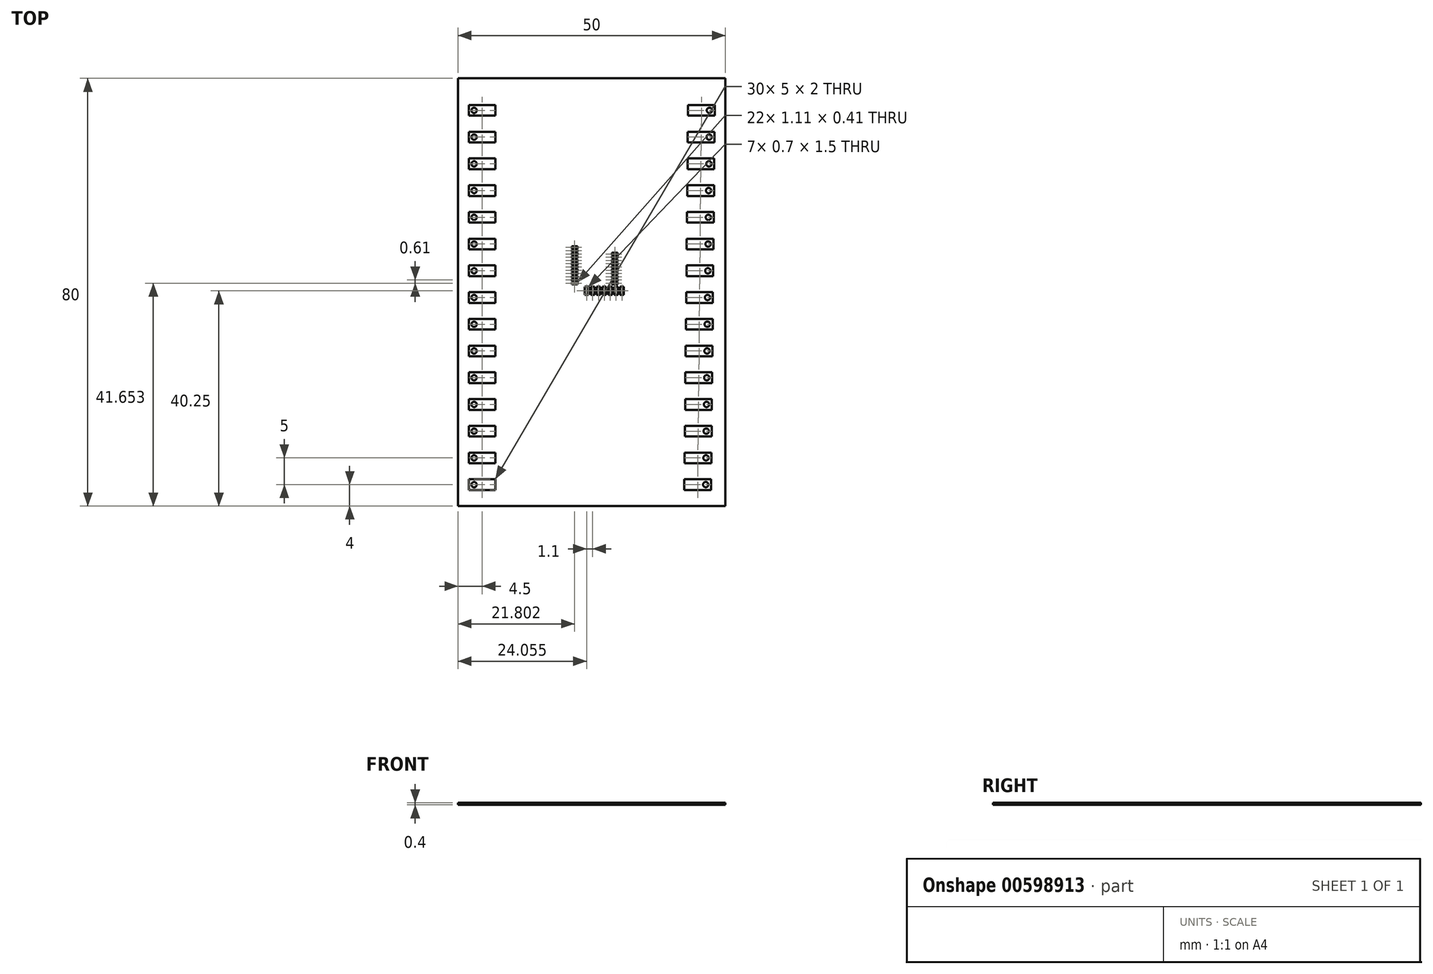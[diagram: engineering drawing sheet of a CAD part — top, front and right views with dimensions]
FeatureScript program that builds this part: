
annotation { "Feature Type Name" : "Feature", "Feature Type Description" : "" }
export const myFeature = defineFeature(function(context is Context, id is Id, definition is map)
    precondition{}
    {
        {
            var Q0;
            Q0=qCreatedBy(makeId("Top.planeOp"),FACE);
            var sketch = newSketch(context, id + "F0", { "sketchPlane" : qUnion([Q0])});
            skLineSegment(sketch, "E0.bottom", {"start": v(-25, 40) * mm, "end": v(25, 40) * mm});
            skLineSegment(sketch, "E0.top", {"start": v(-25, -40) * mm, "end": v(25, -40) * mm});
            skLineSegment(sketch, "E0.left", {"start": v(-25, 40) * mm, "end": v(-25, -40) * mm});
            skLineSegment(sketch, "E0.right", {"start": v(25, 40) * mm, "end": v(25, -40) * mm});
            skSolve(sketch);
        }
        {
            var Q0;
            Q0=makeQuery(id+"F0.imprint","IMPRINT",FACE,{"disambiguationData":[TD([[makeQuery(id+"F0.imprint","IMPRINT",EDGE,{"derivedFrom":sQuery(id+"F0.wireOp",EDGE,"E0.bottom")}),-1.0]])]});
            extrude(context, id + "F1", {"entities" : qUnion([Q0]), "depth" : .4 * mm, "offsetDistance" : 25 * mm});
        }
        {
            var Q0;
            Q0=makeQuery(id+"F1.opExtrude","CAP_FACE",FACE,{"disambiguationData":[OSD([sQuery(id+"F0.wireOp",EDGE,"E0.bottom"),sQuery(id+"F0.wireOp",EDGE,"E0.top"),sQuery(id+"F0.wireOp",EDGE,"E0.left"),sQuery(id+"F0.wireOp",EDGE,"E0.right")])],"isStart":false});
            var sketch = newSketch(context, id + "F2", { "sketchPlane" : qUnion([Q0])});
            skLineSegment(sketch, "E1.bottom", {"start": v(-23, 35) * mm, "end": v(-18, 35) * mm});
            skLineSegment(sketch, "E1.top", {"start": v(-23, 33) * mm, "end": v(-18, 33) * mm});
            skLineSegment(sketch, "E1.left", {"start": v(-23, 35) * mm, "end": v(-23, 33) * mm});
            skLineSegment(sketch, "E1.right", {"start": v(-18, 35) * mm, "end": v(-18, 33) * mm});
            skLineSegment(sketch, "E2.1.0.0", {"start": v(-23, 30) * mm, "end": v(-18, 30) * mm});
            skLineSegment(sketch, "E2.1.0.1", {"start": v(-23, 28) * mm, "end": v(-18, 28) * mm});
            skLineSegment(sketch, "E2.1.0.2", {"start": v(-18, 30) * mm, "end": v(-18, 28) * mm});
            skLineSegment(sketch, "E2.1.0.3", {"start": v(-23, 30) * mm, "end": v(-23, 28) * mm});
            skLineSegment(sketch, "E2.2.0.0", {"start": v(-23, 25) * mm, "end": v(-18, 25) * mm});
            skLineSegment(sketch, "E2.2.0.1", {"start": v(-23, 23) * mm, "end": v(-18, 23) * mm});
            skLineSegment(sketch, "E2.2.0.2", {"start": v(-18, 25) * mm, "end": v(-18, 23) * mm});
            skLineSegment(sketch, "E2.2.0.3", {"start": v(-23, 25) * mm, "end": v(-23, 23) * mm});
            skLineSegment(sketch, "E2.3.0.0", {"start": v(-23, 20) * mm, "end": v(-18, 20) * mm});
            skLineSegment(sketch, "E2.3.0.1", {"start": v(-23, 18) * mm, "end": v(-18, 18) * mm});
            skLineSegment(sketch, "E2.3.0.2", {"start": v(-18, 20) * mm, "end": v(-18, 18) * mm});
            skLineSegment(sketch, "E2.3.0.3", {"start": v(-23, 20) * mm, "end": v(-23, 18) * mm});
            skLineSegment(sketch, "E2.4.0.0", {"start": v(-23, 15) * mm, "end": v(-18, 15) * mm});
            skLineSegment(sketch, "E2.4.0.1", {"start": v(-23, 13) * mm, "end": v(-18, 13) * mm});
            skLineSegment(sketch, "E2.4.0.2", {"start": v(-18, 15) * mm, "end": v(-18, 13) * mm});
            skLineSegment(sketch, "E2.4.0.3", {"start": v(-23, 15) * mm, "end": v(-23, 13) * mm});
            skLineSegment(sketch, "E2.5.0.0", {"start": v(-23, 10) * mm, "end": v(-18, 10) * mm});
            skLineSegment(sketch, "E2.5.0.1", {"start": v(-23, 8) * mm, "end": v(-18, 8) * mm});
            skLineSegment(sketch, "E2.5.0.2", {"start": v(-18, 10) * mm, "end": v(-18, 8) * mm});
            skLineSegment(sketch, "E2.5.0.3", {"start": v(-23, 10) * mm, "end": v(-23, 8) * mm});
            skLineSegment(sketch, "E2.6.0.0", {"start": v(-23, 5) * mm, "end": v(-18, 5) * mm});
            skLineSegment(sketch, "E2.6.0.1", {"start": v(-23, 3) * mm, "end": v(-18, 3) * mm});
            skLineSegment(sketch, "E2.6.0.2", {"start": v(-18, 5) * mm, "end": v(-18, 3) * mm});
            skLineSegment(sketch, "E2.6.0.3", {"start": v(-23, 5) * mm, "end": v(-23, 3) * mm});
            skLineSegment(sketch, "E2.7.0.0", {"start": v(-23, 0) * mm, "end": v(-18, 0) * mm});
            skLineSegment(sketch, "E2.7.0.1", {"start": v(-23, -2) * mm, "end": v(-18, -2) * mm});
            skLineSegment(sketch, "E2.7.0.2", {"start": v(-18, 0) * mm, "end": v(-18, -2) * mm});
            skLineSegment(sketch, "E2.7.0.3", {"start": v(-23, 0) * mm, "end": v(-23, -2) * mm});
            skLineSegment(sketch, "E2.8.0.0", {"start": v(-23, -5) * mm, "end": v(-18, -5) * mm});
            skLineSegment(sketch, "E2.8.0.1", {"start": v(-23, -7) * mm, "end": v(-18, -7) * mm});
            skLineSegment(sketch, "E2.8.0.2", {"start": v(-18, -5) * mm, "end": v(-18, -7) * mm});
            skLineSegment(sketch, "E2.8.0.3", {"start": v(-23, -5) * mm, "end": v(-23, -7) * mm});
            skLineSegment(sketch, "E2.9.0.0", {"start": v(-23, -10) * mm, "end": v(-18, -10) * mm});
            skLineSegment(sketch, "E2.9.0.1", {"start": v(-23, -12) * mm, "end": v(-18, -12) * mm});
            skLineSegment(sketch, "E2.9.0.2", {"start": v(-18, -10) * mm, "end": v(-18, -12) * mm});
            skLineSegment(sketch, "E2.9.0.3", {"start": v(-23, -10) * mm, "end": v(-23, -12) * mm});
            skLineSegment(sketch, "E2.10.0.0", {"start": v(-23, -15) * mm, "end": v(-18, -15) * mm});
            skLineSegment(sketch, "E2.10.0.1", {"start": v(-23, -17) * mm, "end": v(-18, -17) * mm});
            skLineSegment(sketch, "E2.10.0.2", {"start": v(-18, -15) * mm, "end": v(-18, -17) * mm});
            skLineSegment(sketch, "E2.10.0.3", {"start": v(-23, -15) * mm, "end": v(-23, -17) * mm});
            skLineSegment(sketch, "E2.11.0.0", {"start": v(-23, -20) * mm, "end": v(-18, -20) * mm});
            skLineSegment(sketch, "E2.11.0.1", {"start": v(-23, -22) * mm, "end": v(-18, -22) * mm});
            skLineSegment(sketch, "E2.11.0.2", {"start": v(-18, -20) * mm, "end": v(-18, -22) * mm});
            skLineSegment(sketch, "E2.11.0.3", {"start": v(-23, -20) * mm, "end": v(-23, -22) * mm});
            skLineSegment(sketch, "E2.12.0.0", {"start": v(-23, -25) * mm, "end": v(-18, -25) * mm});
            skLineSegment(sketch, "E2.12.0.1", {"start": v(-23, -27) * mm, "end": v(-18, -27) * mm});
            skLineSegment(sketch, "E2.12.0.2", {"start": v(-18, -25) * mm, "end": v(-18, -27) * mm});
            skLineSegment(sketch, "E2.12.0.3", {"start": v(-23, -25) * mm, "end": v(-23, -27) * mm});
            skLineSegment(sketch, "E2.13.0.0", {"start": v(-23, -30) * mm, "end": v(-18, -30) * mm});
            skLineSegment(sketch, "E2.13.0.1", {"start": v(-23, -32) * mm, "end": v(-18, -32) * mm});
            skLineSegment(sketch, "E2.13.0.2", {"start": v(-18, -30) * mm, "end": v(-18, -32) * mm});
            skLineSegment(sketch, "E2.13.0.3", {"start": v(-23, -30) * mm, "end": v(-23, -32) * mm});
            skLineSegment(sketch, "E2.14.0.0", {"start": v(-23, -35) * mm, "end": v(-18, -35) * mm});
            skLineSegment(sketch, "E2.14.0.1", {"start": v(-23, -37) * mm, "end": v(-18, -37) * mm});
            skLineSegment(sketch, "E2.14.0.2", {"start": v(-18, -35) * mm, "end": v(-18, -37) * mm});
            skLineSegment(sketch, "E2.14.0.3", {"start": v(-23, -35) * mm, "end": v(-23, -37) * mm});
            skLineSegment(sketch, "E2.direction1", {"start": v(-23, 33) * mm, "end": v(-23, 28) * mm, "construction": true});
            skCircle(sketch, "E3", {"center": v(-22, 34) * mm, "radius": 0.5 * mm});
            skCircle(sketch, "E4.1.0.0", {"center": v(-22, 29) * mm, "radius": 0.5 * mm});
            skCircle(sketch, "E4.2.0.0", {"center": v(-22, 24) * mm, "radius": 0.5 * mm});
            skCircle(sketch, "E4.3.0.0", {"center": v(-22, 19) * mm, "radius": 0.5 * mm});
            skCircle(sketch, "E4.4.0.0", {"center": v(-22, 14) * mm, "radius": 0.5 * mm});
            skCircle(sketch, "E4.5.0.0", {"center": v(-22, 9) * mm, "radius": 0.5 * mm});
            skCircle(sketch, "E4.6.0.0", {"center": v(-22, 4) * mm, "radius": 0.5 * mm});
            skCircle(sketch, "E4.7.0.0", {"center": v(-22, -1) * mm, "radius": 0.5 * mm});
            skCircle(sketch, "E4.8.0.0", {"center": v(-22, -6) * mm, "radius": 0.5 * mm});
            skCircle(sketch, "E4.9.0.0", {"center": v(-22, -11) * mm, "radius": 0.5 * mm});
            skCircle(sketch, "E4.10.0.0", {"center": v(-22, -16) * mm, "radius": 0.5 * mm});
            skCircle(sketch, "E4.11.0.0", {"center": v(-22, -21) * mm, "radius": 0.5 * mm});
            skCircle(sketch, "E4.12.0.0", {"center": v(-22, -26) * mm, "radius": 0.5 * mm});
            skCircle(sketch, "E4.13.0.0", {"center": v(-22, -31) * mm, "radius": 0.5 * mm});
            skCircle(sketch, "E4.14.0.0", {"center": v(-22, -36) * mm, "radius": 0.5 * mm});
            skLineSegment(sketch, "E4.direction1", {"start": v(-22, 34) * mm, "end": v(-22, 29) * mm, "construction": true});
            skLineSegment(sketch, "E5.bottom", {"start": v(18, 35) * mm, "end": v(23, 35) * mm});
            skLineSegment(sketch, "E5.top", {"start": v(18, 33) * mm, "end": v(23, 33) * mm});
            skLineSegment(sketch, "E5.left", {"start": v(18, 35) * mm, "end": v(18, 33) * mm});
            skLineSegment(sketch, "E5.right", {"start": v(23, 35) * mm, "end": v(23, 33) * mm});
            skCircle(sketch, "E6", {"center": v(22, 34) * mm, "radius": 0.5 * mm});
            skLineSegment(sketch, "E7.1.0.0", {"start": v(17.95, 30) * mm, "end": v(22.95, 30) * mm});
            skLineSegment(sketch, "E7.1.0.1", {"start": v(17.95, 30) * mm, "end": v(17.95, 28) * mm});
            skLineSegment(sketch, "E7.1.0.2", {"start": v(17.95, 28) * mm, "end": v(22.95, 28) * mm});
            skLineSegment(sketch, "E7.1.0.3", {"start": v(22.95, 30) * mm, "end": v(22.95, 28) * mm});
            skCircle(sketch, "E7.1.0.4", {"center": v(21.95, 29) * mm, "radius": 0.5 * mm});
            skLineSegment(sketch, "E7.2.0.0", {"start": v(17.9, 25) * mm, "end": v(22.9, 25) * mm});
            skLineSegment(sketch, "E7.2.0.1", {"start": v(17.9, 25) * mm, "end": v(17.9, 23) * mm});
            skLineSegment(sketch, "E7.2.0.2", {"start": v(17.9, 23) * mm, "end": v(22.9, 23) * mm});
            skLineSegment(sketch, "E7.2.0.3", {"start": v(22.9, 25) * mm, "end": v(22.9, 23) * mm});
            skCircle(sketch, "E7.2.0.4", {"center": v(21.9, 24) * mm, "radius": 0.5 * mm});
            skLineSegment(sketch, "E7.3.0.0", {"start": v(17.85, 20) * mm, "end": v(22.85, 20) * mm});
            skLineSegment(sketch, "E7.3.0.1", {"start": v(17.85, 20) * mm, "end": v(17.85, 18) * mm});
            skLineSegment(sketch, "E7.3.0.2", {"start": v(17.85, 18) * mm, "end": v(22.85, 18) * mm});
            skLineSegment(sketch, "E7.3.0.3", {"start": v(22.85, 20) * mm, "end": v(22.85, 18) * mm});
            skCircle(sketch, "E7.3.0.4", {"center": v(21.85, 19) * mm, "radius": 0.5 * mm});
            skLineSegment(sketch, "E7.4.0.0", {"start": v(17.8, 15) * mm, "end": v(22.8, 15) * mm});
            skLineSegment(sketch, "E7.4.0.1", {"start": v(17.8, 15) * mm, "end": v(17.8, 13) * mm});
            skLineSegment(sketch, "E7.4.0.2", {"start": v(17.8, 13) * mm, "end": v(22.8, 13) * mm});
            skLineSegment(sketch, "E7.4.0.3", {"start": v(22.8, 15) * mm, "end": v(22.8, 13) * mm});
            skCircle(sketch, "E7.4.0.4", {"center": v(21.8, 14) * mm, "radius": 0.5 * mm});
            skLineSegment(sketch, "E7.5.0.0", {"start": v(17.75, 10) * mm, "end": v(22.75, 10) * mm});
            skLineSegment(sketch, "E7.5.0.1", {"start": v(17.75, 10) * mm, "end": v(17.75, 8) * mm});
            skLineSegment(sketch, "E7.5.0.2", {"start": v(17.75, 8) * mm, "end": v(22.75, 8) * mm});
            skLineSegment(sketch, "E7.5.0.3", {"start": v(22.75, 10) * mm, "end": v(22.75, 8) * mm});
            skCircle(sketch, "E7.5.0.4", {"center": v(21.75, 9) * mm, "radius": 0.5 * mm});
            skLineSegment(sketch, "E7.6.0.0", {"start": v(17.7, 5) * mm, "end": v(22.7, 5) * mm});
            skLineSegment(sketch, "E7.6.0.1", {"start": v(17.7, 5) * mm, "end": v(17.7, 3) * mm});
            skLineSegment(sketch, "E7.6.0.2", {"start": v(17.7, 3) * mm, "end": v(22.7, 3) * mm});
            skLineSegment(sketch, "E7.6.0.3", {"start": v(22.7, 5) * mm, "end": v(22.7, 3) * mm});
            skCircle(sketch, "E7.6.0.4", {"center": v(21.7, 4) * mm, "radius": 0.5 * mm});
            skLineSegment(sketch, "E7.7.0.0", {"start": v(17.65, 0) * mm, "end": v(22.65, 0) * mm});
            skLineSegment(sketch, "E7.7.0.1", {"start": v(17.65, 0) * mm, "end": v(17.65, -2) * mm});
            skLineSegment(sketch, "E7.7.0.2", {"start": v(17.65, -2) * mm, "end": v(22.65, -2) * mm});
            skLineSegment(sketch, "E7.7.0.3", {"start": v(22.65, 0) * mm, "end": v(22.65, -2) * mm});
            skCircle(sketch, "E7.7.0.4", {"center": v(21.65, -1) * mm, "radius": 0.5 * mm});
            skLineSegment(sketch, "E7.8.0.0", {"start": v(17.6, -5) * mm, "end": v(22.6, -5) * mm});
            skLineSegment(sketch, "E7.8.0.1", {"start": v(17.6, -5) * mm, "end": v(17.6, -7) * mm});
            skLineSegment(sketch, "E7.8.0.2", {"start": v(17.6, -7) * mm, "end": v(22.6, -7) * mm});
            skLineSegment(sketch, "E7.8.0.3", {"start": v(22.6, -5) * mm, "end": v(22.6, -7) * mm});
            skCircle(sketch, "E7.8.0.4", {"center": v(21.6, -6) * mm, "radius": 0.5 * mm});
            skLineSegment(sketch, "E7.9.0.0", {"start": v(17.55, -10) * mm, "end": v(22.55, -10) * mm});
            skLineSegment(sketch, "E7.9.0.1", {"start": v(17.55, -10) * mm, "end": v(17.55, -12) * mm});
            skLineSegment(sketch, "E7.9.0.2", {"start": v(17.55, -12) * mm, "end": v(22.55, -12) * mm});
            skLineSegment(sketch, "E7.9.0.3", {"start": v(22.55, -10) * mm, "end": v(22.55, -12) * mm});
            skCircle(sketch, "E7.9.0.4", {"center": v(21.55, -11) * mm, "radius": 0.5 * mm});
            skLineSegment(sketch, "E7.10.0.0", {"start": v(17.5, -15) * mm, "end": v(22.5, -15) * mm});
            skLineSegment(sketch, "E7.10.0.1", {"start": v(17.5, -15) * mm, "end": v(17.5, -17) * mm});
            skLineSegment(sketch, "E7.10.0.2", {"start": v(17.5, -17) * mm, "end": v(22.5, -17) * mm});
            skLineSegment(sketch, "E7.10.0.3", {"start": v(22.5, -15) * mm, "end": v(22.5, -17) * mm});
            skCircle(sketch, "E7.10.0.4", {"center": v(21.5, -16) * mm, "radius": 0.5 * mm});
            skLineSegment(sketch, "E7.11.0.0", {"start": v(17.46, -20) * mm, "end": v(22.46, -20) * mm});
            skLineSegment(sketch, "E7.11.0.1", {"start": v(17.46, -20) * mm, "end": v(17.46, -22) * mm});
            skLineSegment(sketch, "E7.11.0.2", {"start": v(17.46, -22) * mm, "end": v(22.46, -22) * mm});
            skLineSegment(sketch, "E7.11.0.3", {"start": v(22.46, -20) * mm, "end": v(22.46, -22) * mm});
            skCircle(sketch, "E7.11.0.4", {"center": v(21.46, -21) * mm, "radius": 0.5 * mm});
            skLineSegment(sketch, "E7.12.0.0", {"start": v(17.4, -25) * mm, "end": v(22.4, -25) * mm});
            skLineSegment(sketch, "E7.12.0.1", {"start": v(17.4, -25) * mm, "end": v(17.4, -27) * mm});
            skLineSegment(sketch, "E7.12.0.2", {"start": v(17.4, -27) * mm, "end": v(22.4, -27) * mm});
            skLineSegment(sketch, "E7.12.0.3", {"start": v(22.4, -25) * mm, "end": v(22.4, -27) * mm});
            skCircle(sketch, "E7.12.0.4", {"center": v(21.4, -26) * mm, "radius": 0.5 * mm});
            skLineSegment(sketch, "E7.13.0.0", {"start": v(17.36, -30) * mm, "end": v(22.36, -30) * mm});
            skLineSegment(sketch, "E7.13.0.1", {"start": v(17.36, -30) * mm, "end": v(17.36, -32) * mm});
            skLineSegment(sketch, "E7.13.0.2", {"start": v(17.36, -32) * mm, "end": v(22.36, -32) * mm});
            skLineSegment(sketch, "E7.13.0.3", {"start": v(22.36, -30) * mm, "end": v(22.36, -32) * mm});
            skCircle(sketch, "E7.13.0.4", {"center": v(21.36, -31) * mm, "radius": 0.5 * mm});
            skLineSegment(sketch, "E7.14.0.0", {"start": v(17.3, -35) * mm, "end": v(22.3, -35) * mm});
            skLineSegment(sketch, "E7.14.0.1", {"start": v(17.3, -35) * mm, "end": v(17.3, -37) * mm});
            skLineSegment(sketch, "E7.14.0.2", {"start": v(17.3, -37) * mm, "end": v(22.3, -37) * mm});
            skLineSegment(sketch, "E7.14.0.3", {"start": v(22.3, -35) * mm, "end": v(22.3, -37) * mm});
            skCircle(sketch, "E7.14.0.4", {"center": v(21.3, -36) * mm, "radius": 0.5 * mm});
            skLineSegment(sketch, "E7.direction1", {"start": v(18, 33) * mm, "end": v(17.95, 28) * mm, "construction": true});
            skSolve(sketch);
        }
        {
            var Q0;
            Q0=makeQuery(id+"F2.imprint","IMPRINT",FACE,{"disambiguationData":[TD([[makeQuery(id+"F2.imprint","IMPRINT",EDGE,{"derivedFrom":sQuery(id+"F2.wireOp",EDGE,"E2.14.0.0")}),-1.0]])]});
            var Q1;
            Q1=makeQuery(id+"F2.imprint","IMPRINT",FACE,{"disambiguationData":[TD([[makeQuery(id+"F2.imprint","IMPRINT",EDGE,{"derivedFrom":sQuery(id+"F2.wireOp",EDGE,"E2.13.0.0")}),-1.0]])]});
            var Q2;
            Q2=makeQuery(id+"F2.imprint","IMPRINT",FACE,{"disambiguationData":[TD([[makeQuery(id+"F2.imprint","IMPRINT",EDGE,{"derivedFrom":sQuery(id+"F2.wireOp",EDGE,"E2.12.0.0")}),-1.0]])]});
            var Q3;
            Q3=makeQuery(id+"F2.imprint","IMPRINT",FACE,{"disambiguationData":[TD([[makeQuery(id+"F2.imprint","IMPRINT",EDGE,{"derivedFrom":sQuery(id+"F2.wireOp",EDGE,"E2.11.0.0")}),-1.0]])]});
            var Q4;
            Q4=makeQuery(id+"F2.imprint","IMPRINT",FACE,{"disambiguationData":[TD([[makeQuery(id+"F2.imprint","IMPRINT",EDGE,{"derivedFrom":sQuery(id+"F2.wireOp",EDGE,"E2.10.0.0")}),-1.0]])]});
            var Q5;
            Q5=makeQuery(id+"F2.imprint","IMPRINT",FACE,{"disambiguationData":[TD([[makeQuery(id+"F2.imprint","IMPRINT",EDGE,{"derivedFrom":sQuery(id+"F2.wireOp",EDGE,"E2.9.0.0")}),-1.0]])]});
            var Q6;
            Q6=makeQuery(id+"F2.imprint","IMPRINT",FACE,{"disambiguationData":[TD([[makeQuery(id+"F2.imprint","IMPRINT",EDGE,{"derivedFrom":sQuery(id+"F2.wireOp",EDGE,"E2.8.0.0")}),-1.0]])]});
            var Q7;
            Q7=makeQuery(id+"F2.imprint","IMPRINT",FACE,{"disambiguationData":[TD([[makeQuery(id+"F2.imprint","IMPRINT",EDGE,{"derivedFrom":sQuery(id+"F2.wireOp",EDGE,"E2.6.0.0")}),-1.0]])]});
            var Q8;
            Q8=makeQuery(id+"F2.imprint","IMPRINT",FACE,{"disambiguationData":[TD([[makeQuery(id+"F2.imprint","IMPRINT",EDGE,{"derivedFrom":sQuery(id+"F2.wireOp",EDGE,"E2.7.0.0")}),-1.0]])]});
            var Q9;
            Q9=makeQuery(id+"F2.imprint","IMPRINT",FACE,{"disambiguationData":[TD([[makeQuery(id+"F2.imprint","IMPRINT",EDGE,{"derivedFrom":sQuery(id+"F2.wireOp",EDGE,"E2.5.0.0")}),-1.0]])]});
            var Q10;
            Q10=makeQuery(id+"F2.imprint","IMPRINT",FACE,{"disambiguationData":[TD([[makeQuery(id+"F2.imprint","IMPRINT",EDGE,{"derivedFrom":sQuery(id+"F2.wireOp",EDGE,"E2.4.0.0")}),-1.0]])]});
            var Q11;
            Q11=makeQuery(id+"F2.imprint","IMPRINT",FACE,{"disambiguationData":[TD([[makeQuery(id+"F2.imprint","IMPRINT",EDGE,{"derivedFrom":sQuery(id+"F2.wireOp",EDGE,"E2.3.0.0")}),-1.0]])]});
            var Q12;
            Q12=makeQuery(id+"F2.imprint","IMPRINT",FACE,{"disambiguationData":[TD([[makeQuery(id+"F2.imprint","IMPRINT",EDGE,{"derivedFrom":sQuery(id+"F2.wireOp",EDGE,"E2.2.0.0")}),-1.0]])]});
            var Q13;
            Q13=makeQuery(id+"F2.imprint","IMPRINT",FACE,{"disambiguationData":[TD([[makeQuery(id+"F2.imprint","IMPRINT",EDGE,{"derivedFrom":sQuery(id+"F2.wireOp",EDGE,"E2.1.0.0")}),-1.0]])]});
            var Q14;
            Q14=makeQuery(id+"F2.imprint","IMPRINT",FACE,{"disambiguationData":[TD([[makeQuery(id+"F2.imprint","IMPRINT",EDGE,{"derivedFrom":sQuery(id+"F2.wireOp",EDGE,"E1.bottom")}),-1.0]])]});
            var Q15;
            Q15=makeQuery(id+"F2.imprint","IMPRINT",FACE,{"disambiguationData":[TD([[makeQuery(id+"F2.imprint","IMPRINT",EDGE,{"derivedFrom":sQuery(id+"F2.wireOp",EDGE,"E7.14.0.0")}),-1.0]])]});
            var Q16;
            Q16=makeQuery(id+"F2.imprint","IMPRINT",FACE,{"disambiguationData":[TD([[makeQuery(id+"F2.imprint","IMPRINT",EDGE,{"derivedFrom":sQuery(id+"F2.wireOp",EDGE,"E7.13.0.0")}),-1.0]])]});
            var Q17;
            Q17=makeQuery(id+"F2.imprint","IMPRINT",FACE,{"disambiguationData":[TD([[makeQuery(id+"F2.imprint","IMPRINT",EDGE,{"derivedFrom":sQuery(id+"F2.wireOp",EDGE,"E7.12.0.0")}),-1.0]])]});
            var Q18;
            Q18=makeQuery(id+"F2.imprint","IMPRINT",FACE,{"disambiguationData":[TD([[makeQuery(id+"F2.imprint","IMPRINT",EDGE,{"derivedFrom":sQuery(id+"F2.wireOp",EDGE,"E7.11.0.0")}),-1.0]])]});
            var Q19;
            Q19=makeQuery(id+"F2.imprint","IMPRINT",FACE,{"disambiguationData":[TD([[makeQuery(id+"F2.imprint","IMPRINT",EDGE,{"derivedFrom":sQuery(id+"F2.wireOp",EDGE,"E7.10.0.0")}),-1.0]])]});
            var Q20;
            Q20=makeQuery(id+"F2.imprint","IMPRINT",FACE,{"disambiguationData":[TD([[makeQuery(id+"F2.imprint","IMPRINT",EDGE,{"derivedFrom":sQuery(id+"F2.wireOp",EDGE,"E7.9.0.0")}),-1.0]])]});
            var Q21;
            Q21=makeQuery(id+"F2.imprint","IMPRINT",FACE,{"disambiguationData":[TD([[makeQuery(id+"F2.imprint","IMPRINT",EDGE,{"derivedFrom":sQuery(id+"F2.wireOp",EDGE,"E7.8.0.0")}),-1.0]])]});
            var Q22;
            Q22=makeQuery(id+"F2.imprint","IMPRINT",FACE,{"disambiguationData":[TD([[makeQuery(id+"F2.imprint","IMPRINT",EDGE,{"derivedFrom":sQuery(id+"F2.wireOp",EDGE,"E7.7.0.0")}),-1.0]])]});
            var Q23;
            Q23=makeQuery(id+"F2.imprint","IMPRINT",FACE,{"disambiguationData":[TD([[makeQuery(id+"F2.imprint","IMPRINT",EDGE,{"derivedFrom":sQuery(id+"F2.wireOp",EDGE,"E7.6.0.0")}),-1.0]])]});
            var Q24;
            Q24=makeQuery(id+"F2.imprint","IMPRINT",FACE,{"disambiguationData":[TD([[makeQuery(id+"F2.imprint","IMPRINT",EDGE,{"derivedFrom":sQuery(id+"F2.wireOp",EDGE,"E7.5.0.0")}),-1.0]])]});
            var Q25;
            Q25=makeQuery(id+"F2.imprint","IMPRINT",FACE,{"disambiguationData":[TD([[makeQuery(id+"F2.imprint","IMPRINT",EDGE,{"derivedFrom":sQuery(id+"F2.wireOp",EDGE,"E7.4.0.0")}),-1.0]])]});
            var Q26;
            Q26=makeQuery(id+"F2.imprint","IMPRINT",FACE,{"disambiguationData":[TD([[makeQuery(id+"F2.imprint","IMPRINT",EDGE,{"derivedFrom":sQuery(id+"F2.wireOp",EDGE,"E7.3.0.0")}),-1.0]])]});
            var Q27;
            Q27=makeQuery(id+"F2.imprint","IMPRINT",FACE,{"disambiguationData":[TD([[makeQuery(id+"F2.imprint","IMPRINT",EDGE,{"derivedFrom":sQuery(id+"F2.wireOp",EDGE,"E7.2.0.0")}),-1.0]])]});
            var Q28;
            Q28=makeQuery(id+"F2.imprint","IMPRINT",FACE,{"disambiguationData":[TD([[makeQuery(id+"F2.imprint","IMPRINT",EDGE,{"derivedFrom":sQuery(id+"F2.wireOp",EDGE,"E7.1.0.0")}),-1.0]])]});
            var Q29;
            Q29=makeQuery(id+"F2.imprint","IMPRINT",FACE,{"disambiguationData":[TD([[makeQuery(id+"F2.imprint","IMPRINT",EDGE,{"derivedFrom":sQuery(id+"F2.wireOp",EDGE,"E5.bottom")}),-1.0]])]});
            extrude(context, id + "F3", {"entities" : qUnion([Q0, Q1, Q2, Q3, Q4, Q5, Q6, Q7, Q8, Q9, Q10, Q11, Q12, Q13, Q14, Q15, Q16, Q17, Q18, Q19, Q20, Q21, Q22, Q23, Q24, Q25, Q26, Q27, Q28, Q29]), "operationType" : NewBodyOperationType.REMOVE, "oppositeDirection" : true, "depth" : .4 * mm, "offsetDistance" : 25 * mm});
        }
        {
            var Q0;
            {var subQ0=sQuery(id+"F0.wireOp",EDGE,"E0.top");var subQ1=sQuery(id+"F0.wireOp",EDGE,"E0.right");var subQ2=sQuery(id+"F0.wireOp",EDGE,"E0.bottom");var subQ3=sQuery(id+"F0.wireOp",EDGE,"E0.left");Q0=makeQuery(id+"F3.boolean.opBoolean","SPLIT",FACE,{"disambiguationData":[TD([makeQuery(id+"F1.opExtrude","SWEPT_FACE",FACE,{"disambiguationData":[OSD([subQ2])]})])],"derivedFrom":makeQuery(id+"F1.opExtrude","CAP_FACE",FACE,{"disambiguationData":[OSD([subQ2,subQ0,subQ3,subQ1])],"isStart":false})});}
            var sketch = newSketch(context, id + "F4", { "sketchPlane" : qUnion([Q0])});
            skLineSegment(sketch, "E8.bottom", {"start": v(-3.75, 1.86) * mm, "end": v(-2.65, 1.86) * mm});
            skLineSegment(sketch, "E8.top", {"start": v(-3.75, 1.45) * mm, "end": v(-2.65, 1.45) * mm});
            skLineSegment(sketch, "E8.left", {"start": v(-3.75, 1.86) * mm, "end": v(-3.75, 1.45) * mm});
            skLineSegment(sketch, "E8.right", {"start": v(-2.65, 1.86) * mm, "end": v(-2.65, 1.45) * mm});
            skLineSegment(sketch, "E9.0.1.0", {"start": v(-3.75, 2.47) * mm, "end": v(-3.75, 2.06) * mm});
            skLineSegment(sketch, "E9.0.1.1", {"start": v(-3.75, 2.47) * mm, "end": v(-2.65, 2.47) * mm});
            skLineSegment(sketch, "E9.0.1.2", {"start": v(-3.75, 2.06) * mm, "end": v(-2.65, 2.06) * mm});
            skLineSegment(sketch, "E9.0.1.3", {"start": v(-2.65, 2.47) * mm, "end": v(-2.65, 2.06) * mm});
            skLineSegment(sketch, "E9.0.2.0", {"start": v(-3.75, 3.08) * mm, "end": v(-3.75, 2.67) * mm});
            skLineSegment(sketch, "E9.0.2.1", {"start": v(-3.75, 3.08) * mm, "end": v(-2.65, 3.08) * mm});
            skLineSegment(sketch, "E9.0.2.2", {"start": v(-3.75, 2.67) * mm, "end": v(-2.65, 2.67) * mm});
            skLineSegment(sketch, "E9.0.2.3", {"start": v(-2.65, 3.08) * mm, "end": v(-2.65, 2.67) * mm});
            skLineSegment(sketch, "E9.0.3.0", {"start": v(-3.75, 3.69) * mm, "end": v(-3.75, 3.28) * mm});
            skLineSegment(sketch, "E9.0.3.1", {"start": v(-3.75, 3.69) * mm, "end": v(-2.65, 3.69) * mm});
            skLineSegment(sketch, "E9.0.3.2", {"start": v(-3.75, 3.28) * mm, "end": v(-2.65, 3.28) * mm});
            skLineSegment(sketch, "E9.0.3.3", {"start": v(-2.65, 3.69) * mm, "end": v(-2.65, 3.28) * mm});
            skLineSegment(sketch, "E9.0.4.0", {"start": v(-3.75, 4.3) * mm, "end": v(-3.75, 3.89) * mm});
            skLineSegment(sketch, "E9.0.4.1", {"start": v(-3.75, 4.3) * mm, "end": v(-2.65, 4.3) * mm});
            skLineSegment(sketch, "E9.0.4.2", {"start": v(-3.75, 3.89) * mm, "end": v(-2.65, 3.89) * mm});
            skLineSegment(sketch, "E9.0.4.3", {"start": v(-2.65, 4.3) * mm, "end": v(-2.65, 3.89) * mm});
            skLineSegment(sketch, "E9.0.5.0", {"start": v(-3.75, 4.9) * mm, "end": v(-3.75, 4.5) * mm});
            skLineSegment(sketch, "E9.0.5.1", {"start": v(-3.75, 4.9) * mm, "end": v(-2.65, 4.9) * mm});
            skLineSegment(sketch, "E9.0.5.2", {"start": v(-3.75, 4.5) * mm, "end": v(-2.65, 4.5) * mm});
            skLineSegment(sketch, "E9.0.5.3", {"start": v(-2.65, 4.9) * mm, "end": v(-2.65, 4.5) * mm});
            skLineSegment(sketch, "E9.0.6.0", {"start": v(-3.75, 5.52) * mm, "end": v(-3.75, 5.1) * mm});
            skLineSegment(sketch, "E9.0.6.1", {"start": v(-3.75, 5.52) * mm, "end": v(-2.65, 5.52) * mm});
            skLineSegment(sketch, "E9.0.6.2", {"start": v(-3.75, 5.1) * mm, "end": v(-2.65, 5.11) * mm});
            skLineSegment(sketch, "E9.0.6.3", {"start": v(-2.65, 5.52) * mm, "end": v(-2.65, 5.11) * mm});
            skLineSegment(sketch, "E9.0.7.0", {"start": v(-3.75, 6.13) * mm, "end": v(-3.75, 5.72) * mm});
            skLineSegment(sketch, "E9.0.7.1", {"start": v(-3.75, 6.13) * mm, "end": v(-2.65, 6.13) * mm});
            skLineSegment(sketch, "E9.0.7.2", {"start": v(-3.75, 5.72) * mm, "end": v(-2.65, 5.72) * mm});
            skLineSegment(sketch, "E9.0.7.3", {"start": v(-2.65, 6.13) * mm, "end": v(-2.65, 5.72) * mm});
            skLineSegment(sketch, "E9.0.8.0", {"start": v(-3.75, 6.74) * mm, "end": v(-3.75, 6.33) * mm});
            skLineSegment(sketch, "E9.0.8.1", {"start": v(-3.75, 6.74) * mm, "end": v(-2.65, 6.74) * mm});
            skLineSegment(sketch, "E9.0.8.2", {"start": v(-3.75, 6.33) * mm, "end": v(-2.65, 6.33) * mm});
            skLineSegment(sketch, "E9.0.8.3", {"start": v(-2.65, 6.74) * mm, "end": v(-2.65, 6.33) * mm});
            skLineSegment(sketch, "E9.0.9.0", {"start": v(-3.75, 7.35) * mm, "end": v(-3.75, 6.94) * mm});
            skLineSegment(sketch, "E9.0.9.1", {"start": v(-3.75, 7.35) * mm, "end": v(-2.65, 7.35) * mm});
            skLineSegment(sketch, "E9.0.9.2", {"start": v(-3.75, 6.94) * mm, "end": v(-2.65, 6.94) * mm});
            skLineSegment(sketch, "E9.0.9.3", {"start": v(-2.65, 7.35) * mm, "end": v(-2.65, 6.94) * mm});
            skLineSegment(sketch, "E9.0.10.0", {"start": v(-3.75, 7.96) * mm, "end": v(-3.75, 7.55) * mm});
            skLineSegment(sketch, "E9.0.10.1", {"start": v(-3.75, 7.96) * mm, "end": v(-2.65, 7.96) * mm});
            skLineSegment(sketch, "E9.0.10.2", {"start": v(-3.75, 7.55) * mm, "end": v(-2.65, 7.55) * mm});
            skLineSegment(sketch, "E9.0.10.3", {"start": v(-2.65, 7.96) * mm, "end": v(-2.65, 7.55) * mm});
            skLineSegment(sketch, "E9.0.11.0", {"start": v(-3.75, 8.57) * mm, "end": v(-3.75, 8.16) * mm});
            skLineSegment(sketch, "E9.0.11.1", {"start": v(-3.75, 8.57) * mm, "end": v(-2.65, 8.57) * mm});
            skLineSegment(sketch, "E9.0.11.2", {"start": v(-3.75, 8.16) * mm, "end": v(-2.65, 8.16) * mm});
            skLineSegment(sketch, "E9.0.11.3", {"start": v(-2.65, 8.57) * mm, "end": v(-2.65, 8.16) * mm});
            skLineSegment(sketch, "E9.1.0.0", {"start": v(3.75, 1.86) * mm, "end": v(3.75, 1.45) * mm});
            skLineSegment(sketch, "E9.1.0.1", {"start": v(3.75, 1.86) * mm, "end": v(4.86, 1.86) * mm});
            skLineSegment(sketch, "E9.1.0.2", {"start": v(3.75, 1.45) * mm, "end": v(4.86, 1.45) * mm});
            skLineSegment(sketch, "E9.1.0.3", {"start": v(4.86, 1.86) * mm, "end": v(4.86, 1.45) * mm});
            skLineSegment(sketch, "E9.1.1.0", {"start": v(3.75, 2.47) * mm, "end": v(3.75, 2.06) * mm});
            skLineSegment(sketch, "E9.1.1.1", {"start": v(3.75, 2.47) * mm, "end": v(4.86, 2.47) * mm});
            skLineSegment(sketch, "E9.1.1.2", {"start": v(3.75, 2.06) * mm, "end": v(4.86, 2.06) * mm});
            skLineSegment(sketch, "E9.1.1.3", {"start": v(4.86, 2.47) * mm, "end": v(4.86, 2.06) * mm});
            skLineSegment(sketch, "E9.1.2.0", {"start": v(3.75, 3.08) * mm, "end": v(3.75, 2.67) * mm});
            skLineSegment(sketch, "E9.1.2.1", {"start": v(3.75, 3.08) * mm, "end": v(4.86, 3.08) * mm});
            skLineSegment(sketch, "E9.1.2.2", {"start": v(3.75, 2.67) * mm, "end": v(4.86, 2.67) * mm});
            skLineSegment(sketch, "E9.1.2.3", {"start": v(4.86, 3.08) * mm, "end": v(4.86, 2.67) * mm});
            skLineSegment(sketch, "E9.1.3.0", {"start": v(3.75, 3.69) * mm, "end": v(3.75, 3.28) * mm});
            skLineSegment(sketch, "E9.1.3.1", {"start": v(3.75, 3.69) * mm, "end": v(4.86, 3.69) * mm});
            skLineSegment(sketch, "E9.1.3.2", {"start": v(3.75, 3.28) * mm, "end": v(4.86, 3.28) * mm});
            skLineSegment(sketch, "E9.1.3.3", {"start": v(4.86, 3.69) * mm, "end": v(4.86, 3.28) * mm});
            skLineSegment(sketch, "E9.1.4.0", {"start": v(3.75, 4.3) * mm, "end": v(3.75, 3.89) * mm});
            skLineSegment(sketch, "E9.1.4.1", {"start": v(3.75, 4.3) * mm, "end": v(4.86, 4.3) * mm});
            skLineSegment(sketch, "E9.1.4.2", {"start": v(3.75, 3.89) * mm, "end": v(4.86, 3.89) * mm});
            skLineSegment(sketch, "E9.1.4.3", {"start": v(4.86, 4.3) * mm, "end": v(4.86, 3.89) * mm});
            skLineSegment(sketch, "E9.1.5.0", {"start": v(3.75, 4.9) * mm, "end": v(3.75, 4.5) * mm});
            skLineSegment(sketch, "E9.1.5.1", {"start": v(3.75, 4.9) * mm, "end": v(4.86, 4.9) * mm});
            skLineSegment(sketch, "E9.1.5.2", {"start": v(3.75, 4.5) * mm, "end": v(4.86, 4.5) * mm});
            skLineSegment(sketch, "E9.1.5.3", {"start": v(4.86, 4.9) * mm, "end": v(4.86, 4.5) * mm});
            skLineSegment(sketch, "E9.1.6.0", {"start": v(3.75, 5.52) * mm, "end": v(3.75, 5.1) * mm});
            skLineSegment(sketch, "E9.1.6.1", {"start": v(3.75, 5.52) * mm, "end": v(4.86, 5.52) * mm});
            skLineSegment(sketch, "E9.1.6.2", {"start": v(3.75, 5.1) * mm, "end": v(4.86, 5.1) * mm});
            skLineSegment(sketch, "E9.1.6.3", {"start": v(4.86, 5.52) * mm, "end": v(4.86, 5.11) * mm});
            skLineSegment(sketch, "E9.1.7.0", {"start": v(3.75, 6.13) * mm, "end": v(3.75, 5.72) * mm});
            skLineSegment(sketch, "E9.1.7.1", {"start": v(3.75, 6.13) * mm, "end": v(4.86, 6.13) * mm});
            skLineSegment(sketch, "E9.1.7.2", {"start": v(3.75, 5.72) * mm, "end": v(4.86, 5.72) * mm});
            skLineSegment(sketch, "E9.1.7.3", {"start": v(4.86, 6.13) * mm, "end": v(4.86, 5.72) * mm});
            skLineSegment(sketch, "E9.1.8.0", {"start": v(3.75, 6.74) * mm, "end": v(3.75, 6.33) * mm});
            skLineSegment(sketch, "E9.1.8.1", {"start": v(3.75, 6.74) * mm, "end": v(4.86, 6.74) * mm});
            skLineSegment(sketch, "E9.1.8.2", {"start": v(3.75, 6.33) * mm, "end": v(4.86, 6.33) * mm});
            skLineSegment(sketch, "E9.1.8.3", {"start": v(4.86, 6.74) * mm, "end": v(4.86, 6.33) * mm});
            skLineSegment(sketch, "E9.1.9.0", {"start": v(3.75, 7.35) * mm, "end": v(3.75, 6.94) * mm});
            skLineSegment(sketch, "E9.1.9.1", {"start": v(3.75, 7.35) * mm, "end": v(4.86, 7.35) * mm});
            skLineSegment(sketch, "E9.1.9.2", {"start": v(3.75, 6.94) * mm, "end": v(4.86, 6.94) * mm});
            skLineSegment(sketch, "E9.1.9.3", {"start": v(4.86, 7.35) * mm, "end": v(4.86, 6.94) * mm});
            skLineSegment(sketch, "E9.1.10.0", {"start": v(3.75, 7.96) * mm, "end": v(3.75, 7.55) * mm});
            skLineSegment(sketch, "E9.1.10.1", {"start": v(3.75, 7.96) * mm, "end": v(4.86, 7.96) * mm});
            skLineSegment(sketch, "E9.1.10.2", {"start": v(3.75, 7.55) * mm, "end": v(4.86, 7.55) * mm});
            skLineSegment(sketch, "E9.1.10.3", {"start": v(4.86, 7.96) * mm, "end": v(4.86, 7.55) * mm});
            skLineSegment(sketch, "E9.1.11.0", {"start": v(3.75, 8.57) * mm, "end": v(3.75, 8.16) * mm});
            skLineSegment(sketch, "E9.1.11.1", {"start": v(3.75, 8.57) * mm, "end": v(4.86, 8.57) * mm});
            skLineSegment(sketch, "E9.1.11.2", {"start": v(3.75, 8.16) * mm, "end": v(4.86, 8.16) * mm});
            skLineSegment(sketch, "E9.1.11.3", {"start": v(4.86, 8.57) * mm, "end": v(4.86, 8.16) * mm});
            skLineSegment(sketch, "E9.direction1", {"start": v(-3.75, 1.45) * mm, "end": v(3.75, 1.45) * mm, "construction": true});
            skLineSegment(sketch, "E9.direction2", {"start": v(-3.75, 1.45) * mm, "end": v(-3.75, 2.06) * mm, "construction": true});
            skLineSegment(sketch, "E10.bottom", {"start": v(-1.3, 1) * mm, "end": v(-0.6, 1) * mm});
            skLineSegment(sketch, "E10.top", {"start": v(-1.3, -0.5) * mm, "end": v(-0.6, -0.5) * mm});
            skLineSegment(sketch, "E10.left", {"start": v(-1.3, 1) * mm, "end": v(-1.3, -0.5) * mm});
            skLineSegment(sketch, "E10.right", {"start": v(-0.6, 1) * mm, "end": v(-0.6, -0.5) * mm});
            skLineSegment(sketch, "E11.1.0.0", {"start": v(-0.2, 1) * mm, "end": v(-0.2, -0.5) * mm});
            skLineSegment(sketch, "E11.1.0.1", {"start": v(-0.2, -0.5) * mm, "end": v(0.5, -0.5) * mm});
            skLineSegment(sketch, "E11.1.0.2", {"start": v(0.5, 1) * mm, "end": v(0.5, -0.5) * mm});
            skLineSegment(sketch, "E11.1.0.3", {"start": v(-0.2, 1) * mm, "end": v(0.5, 1) * mm});
            skLineSegment(sketch, "E11.2.0.0", {"start": v(0.9, 1) * mm, "end": v(0.9, -0.5) * mm});
            skLineSegment(sketch, "E11.2.0.1", {"start": v(0.9, -0.5) * mm, "end": v(1.6, -0.5) * mm});
            skLineSegment(sketch, "E11.2.0.2", {"start": v(1.6, 1) * mm, "end": v(1.6, -0.5) * mm});
            skLineSegment(sketch, "E11.2.0.3", {"start": v(0.9, 1) * mm, "end": v(1.6, 1) * mm});
            skLineSegment(sketch, "E11.3.0.0", {"start": v(2, 1) * mm, "end": v(2, -0.5) * mm});
            skLineSegment(sketch, "E11.3.0.1", {"start": v(2, -0.5) * mm, "end": v(2.7, -0.5) * mm});
            skLineSegment(sketch, "E11.3.0.2", {"start": v(2.7, 1) * mm, "end": v(2.7, -0.5) * mm});
            skLineSegment(sketch, "E11.3.0.3", {"start": v(2, 1) * mm, "end": v(2.7, 1) * mm});
            skLineSegment(sketch, "E11.4.0.0", {"start": v(3.1, 1) * mm, "end": v(3.1, -0.5) * mm});
            skLineSegment(sketch, "E11.4.0.1", {"start": v(3.1, -0.5) * mm, "end": v(3.8, -0.5) * mm});
            skLineSegment(sketch, "E11.4.0.2", {"start": v(3.8, 1) * mm, "end": v(3.8, -0.5) * mm});
            skLineSegment(sketch, "E11.4.0.3", {"start": v(3.1, 1) * mm, "end": v(3.8, 1) * mm});
            skLineSegment(sketch, "E11.5.0.0", {"start": v(4.2, 1) * mm, "end": v(4.2, -0.5) * mm});
            skLineSegment(sketch, "E11.5.0.1", {"start": v(4.2, -0.5) * mm, "end": v(4.9, -0.5) * mm});
            skLineSegment(sketch, "E11.5.0.2", {"start": v(4.9, 1) * mm, "end": v(4.9, -0.5) * mm});
            skLineSegment(sketch, "E11.5.0.3", {"start": v(4.2, 1) * mm, "end": v(4.9, 1) * mm});
            skLineSegment(sketch, "E11.6.0.0", {"start": v(5.3, 1) * mm, "end": v(5.3, -0.5) * mm});
            skLineSegment(sketch, "E11.6.0.1", {"start": v(5.3, -0.5) * mm, "end": v(6, -0.5) * mm});
            skLineSegment(sketch, "E11.6.0.2", {"start": v(6, 1) * mm, "end": v(6, -0.5) * mm});
            skLineSegment(sketch, "E11.6.0.3", {"start": v(5.3, 1) * mm, "end": v(6, 1) * mm});
            skLineSegment(sketch, "E11.direction1", {"start": v(-1.3, -0.5) * mm, "end": v(-0.2, -0.5) * mm, "construction": true});
            skSolve(sketch);
        }
        {
            var Q0;
            Q0=makeQuery(id+"F4.imprint","IMPRINT",FACE,{"disambiguationData":[TD([[makeQuery(id+"F4.imprint","IMPRINT",EDGE,{"derivedFrom":sQuery(id+"F4.wireOp",EDGE,"E9.0.11.0")}),1.0]])]});
            var Q1;
            Q1=makeQuery(id+"F4.imprint","IMPRINT",FACE,{"disambiguationData":[TD([[makeQuery(id+"F4.imprint","IMPRINT",EDGE,{"derivedFrom":sQuery(id+"F4.wireOp",EDGE,"E9.0.10.0")}),1.0]])]});
            var Q2;
            Q2=makeQuery(id+"F4.imprint","IMPRINT",FACE,{"disambiguationData":[TD([[makeQuery(id+"F4.imprint","IMPRINT",EDGE,{"derivedFrom":sQuery(id+"F4.wireOp",EDGE,"E9.0.9.0")}),1.0]])]});
            var Q3;
            Q3=makeQuery(id+"F4.imprint","IMPRINT",FACE,{"disambiguationData":[TD([[makeQuery(id+"F4.imprint","IMPRINT",EDGE,{"derivedFrom":sQuery(id+"F4.wireOp",EDGE,"E9.0.8.0")}),1.0]])]});
            var Q4;
            Q4=makeQuery(id+"F4.imprint","IMPRINT",FACE,{"disambiguationData":[TD([[makeQuery(id+"F4.imprint","IMPRINT",EDGE,{"derivedFrom":sQuery(id+"F4.wireOp",EDGE,"E9.0.7.0")}),1.0]])]});
            var Q5;
            Q5=makeQuery(id+"F4.imprint","IMPRINT",FACE,{"disambiguationData":[TD([[makeQuery(id+"F4.imprint","IMPRINT",EDGE,{"derivedFrom":sQuery(id+"F4.wireOp",EDGE,"E9.0.6.0")}),1.0]])]});
            var Q6;
            Q6=makeQuery(id+"F4.imprint","IMPRINT",FACE,{"disambiguationData":[TD([[makeQuery(id+"F4.imprint","IMPRINT",EDGE,{"derivedFrom":sQuery(id+"F4.wireOp",EDGE,"E9.0.5.0")}),1.0]])]});
            var Q7;
            Q7=makeQuery(id+"F4.imprint","IMPRINT",FACE,{"disambiguationData":[TD([[makeQuery(id+"F4.imprint","IMPRINT",EDGE,{"derivedFrom":sQuery(id+"F4.wireOp",EDGE,"E9.0.4.0")}),1.0]])]});
            var Q8;
            Q8=makeQuery(id+"F4.imprint","IMPRINT",FACE,{"disambiguationData":[TD([[makeQuery(id+"F4.imprint","IMPRINT",EDGE,{"derivedFrom":sQuery(id+"F4.wireOp",EDGE,"E9.0.3.0")}),1.0]])]});
            var Q9;
            Q9=makeQuery(id+"F4.imprint","IMPRINT",FACE,{"disambiguationData":[TD([[makeQuery(id+"F4.imprint","IMPRINT",EDGE,{"derivedFrom":sQuery(id+"F4.wireOp",EDGE,"E9.0.2.0")}),1.0]])]});
            var Q10;
            Q10=makeQuery(id+"F4.imprint","IMPRINT",FACE,{"disambiguationData":[TD([[makeQuery(id+"F4.imprint","IMPRINT",EDGE,{"derivedFrom":sQuery(id+"F4.wireOp",EDGE,"E9.0.1.0")}),1.0]])]});
            var Q11;
            Q11=makeQuery(id+"F4.imprint","IMPRINT",FACE,{"disambiguationData":[TD([[makeQuery(id+"F4.imprint","IMPRINT",EDGE,{"derivedFrom":sQuery(id+"F4.wireOp",EDGE,"E8.bottom")}),-1.0]])]});
            var Q12;
            Q12=makeQuery(id+"F4.imprint","IMPRINT",FACE,{"disambiguationData":[TD([[makeQuery(id+"F4.imprint","IMPRINT",EDGE,{"derivedFrom":sQuery(id+"F4.wireOp",EDGE,"E10.bottom")}),-1.0]])]});
            var Q13;
            Q13=makeQuery(id+"F4.imprint","IMPRINT",FACE,{"disambiguationData":[TD([[makeQuery(id+"F4.imprint","IMPRINT",EDGE,{"derivedFrom":sQuery(id+"F4.wireOp",EDGE,"E11.1.0.0")}),1.0]])]});
            var Q14;
            Q14=makeQuery(id+"F4.imprint","IMPRINT",FACE,{"disambiguationData":[TD([[makeQuery(id+"F4.imprint","IMPRINT",EDGE,{"derivedFrom":sQuery(id+"F4.wireOp",EDGE,"E11.2.0.0")}),1.0]])]});
            var Q15;
            Q15=makeQuery(id+"F4.imprint","IMPRINT",FACE,{"disambiguationData":[TD([[makeQuery(id+"F4.imprint","IMPRINT",EDGE,{"derivedFrom":sQuery(id+"F4.wireOp",EDGE,"E11.3.0.0")}),1.0]])]});
            var Q16;
            Q16=makeQuery(id+"F4.imprint","IMPRINT",FACE,{"disambiguationData":[TD([[makeQuery(id+"F4.imprint","IMPRINT",EDGE,{"derivedFrom":sQuery(id+"F4.wireOp",EDGE,"E11.4.0.0")}),1.0]])]});
            var Q17;
            Q17=makeQuery(id+"F4.imprint","IMPRINT",FACE,{"disambiguationData":[TD([[makeQuery(id+"F4.imprint","IMPRINT",EDGE,{"derivedFrom":sQuery(id+"F4.wireOp",EDGE,"E11.5.0.0")}),1.0]])]});
            var Q18;
            Q18=makeQuery(id+"F4.imprint","IMPRINT",FACE,{"disambiguationData":[TD([[makeQuery(id+"F4.imprint","IMPRINT",EDGE,{"derivedFrom":sQuery(id+"F4.wireOp",EDGE,"E11.6.0.0")}),1.0]])]});
            var Q19;
            Q19=makeQuery(id+"F4.imprint","IMPRINT",FACE,{"disambiguationData":[TD([[makeQuery(id+"F4.imprint","IMPRINT",EDGE,{"derivedFrom":sQuery(id+"F4.wireOp",EDGE,"E9.1.0.0")}),1.0]])]});
            var Q20;
            Q20=makeQuery(id+"F4.imprint","IMPRINT",FACE,{"disambiguationData":[TD([[makeQuery(id+"F4.imprint","IMPRINT",EDGE,{"derivedFrom":sQuery(id+"F4.wireOp",EDGE,"E9.1.1.0")}),1.0]])]});
            var Q21;
            Q21=makeQuery(id+"F4.imprint","IMPRINT",FACE,{"disambiguationData":[TD([[makeQuery(id+"F4.imprint","IMPRINT",EDGE,{"derivedFrom":sQuery(id+"F4.wireOp",EDGE,"E9.1.2.0")}),1.0]])]});
            var Q22;
            Q22=makeQuery(id+"F4.imprint","IMPRINT",FACE,{"disambiguationData":[TD([[makeQuery(id+"F4.imprint","IMPRINT",EDGE,{"derivedFrom":sQuery(id+"F4.wireOp",EDGE,"E9.1.3.0")}),1.0]])]});
            var Q23;
            Q23=makeQuery(id+"F4.imprint","IMPRINT",FACE,{"disambiguationData":[TD([[makeQuery(id+"F4.imprint","IMPRINT",EDGE,{"derivedFrom":sQuery(id+"F4.wireOp",EDGE,"E9.1.4.0")}),1.0]])]});
            var Q24;
            Q24=makeQuery(id+"F4.imprint","IMPRINT",FACE,{"disambiguationData":[TD([[makeQuery(id+"F4.imprint","IMPRINT",EDGE,{"derivedFrom":sQuery(id+"F4.wireOp",EDGE,"E9.1.5.0")}),1.0]])]});
            var Q25;
            Q25=makeQuery(id+"F4.imprint","IMPRINT",FACE,{"disambiguationData":[TD([[makeQuery(id+"F4.imprint","IMPRINT",EDGE,{"derivedFrom":sQuery(id+"F4.wireOp",EDGE,"E9.1.6.0")}),1.0]])]});
            var Q26;
            Q26=makeQuery(id+"F4.imprint","IMPRINT",FACE,{"disambiguationData":[TD([[makeQuery(id+"F4.imprint","IMPRINT",EDGE,{"derivedFrom":sQuery(id+"F4.wireOp",EDGE,"E9.1.7.0")}),1.0]])]});
            var Q27;
            Q27=makeQuery(id+"F4.imprint","IMPRINT",FACE,{"disambiguationData":[TD([[makeQuery(id+"F4.imprint","IMPRINT",EDGE,{"derivedFrom":sQuery(id+"F4.wireOp",EDGE,"E9.1.8.0")}),1.0]])]});
            var Q28;
            Q28=makeQuery(id+"F4.imprint","IMPRINT",FACE,{"disambiguationData":[TD([[makeQuery(id+"F4.imprint","IMPRINT",EDGE,{"derivedFrom":sQuery(id+"F4.wireOp",EDGE,"E9.1.9.0")}),1.0]])]});
            extrude(context, id + "F5", {"entities" : qUnion([Q0, Q1, Q2, Q3, Q4, Q5, Q6, Q7, Q8, Q9, Q10, Q11, Q12, Q13, Q14, Q15, Q16, Q17, Q18, Q19, Q20, Q21, Q22, Q23, Q24, Q25, Q26, Q27, Q28]), "operationType" : NewBodyOperationType.REMOVE, "oppositeDirection" : true, "depth" : .4 * mm, "offsetDistance" : 25 * mm});
        }
    });
